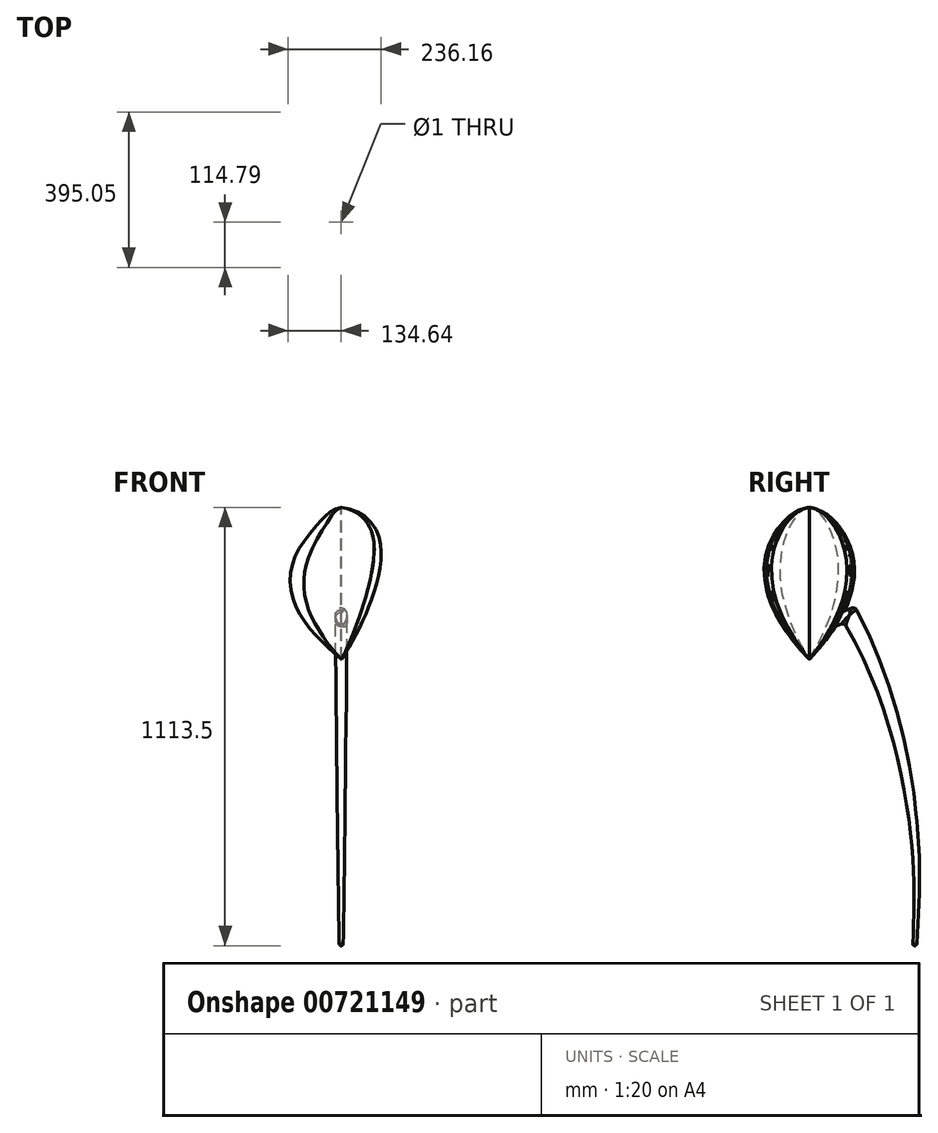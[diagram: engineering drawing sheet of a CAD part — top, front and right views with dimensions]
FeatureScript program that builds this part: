
annotation { "Feature Type Name" : "Feature", "Feature Type Description" : "" }
export const myFeature = defineFeature(function(context is Context, id is Id, definition is map)
    precondition{}
    {
        {
            var Q0;
            Q0=qCreatedBy(makeId("Top.planeOp"),FACE);
            var sketch = newSketch(context, id + "F0", { "sketchPlane" : qUnion([Q0])});
            skCircle(sketch, "E0", {"center": v(0, 0) * mm, "radius": 83.85 * mm, "construction": true});
            skArc(sketch, "E1", {"start": v(12.92, 91.47) * mm, "mid": v(7.44, 96.88) * mm, "end": v(0, 98.85) * mm});
            skLineSegment(sketch, "E2", {"start": v(0, 0) * mm, "end": v(0, 114.42) * mm, "construction": true});
            skLineSegment(sketch, "E3", {"start": v(0, 0) * mm, "end": v(123.6, 0) * mm, "construction": true});
            skArc(sketch, "E4.1.0", {"start": v(40.56, 83) * mm, "mid": v(30.55, 94.01) * mm, "end": v(15.97, 90.98) * mm});
            skArc(sketch, "E4.2.0", {"start": v(64.22, 66.4) * mm, "mid": v(58.1, 79.97) * mm, "end": v(43.3, 81.6) * mm});
            skArc(sketch, "E4.3.0", {"start": v(81.6, 43.3) * mm, "mid": v(79.97, 58.1) * mm, "end": v(66.4, 64.22) * mm});
            skArc(sketch, "E4.4.0", {"start": v(90.98, 15.97) * mm, "mid": v(94.01, 30.55) * mm, "end": v(83, 40.56) * mm});
            skArc(sketch, "E4.5.0", {"start": v(98.85, 0) * mm, "mid": v(96.88, 7.44) * mm, "end": v(91.47, 12.92) * mm});
            skLineSegment(sketch, "E4.anchor1", {"start": v(0, 0) * mm, "end": v(0, 83.85) * mm, "construction": true});
            skLineSegment(sketch, "E4.anchor2", {"start": v(0, 0) * mm, "end": v(83.85, 0) * mm, "construction": true});
            skPoint(sketch, "E5.visualSharp", {"position": v(14.1, 88.99) * mm});
            skArc(sketch, "E5.filletArc", {"start": v(12.92, 91.47) * mm, "mid": v(14.33, 90.5) * mm, "end": v(15.97, 90.98) * mm});
            skPoint(sketch, "E6.visualSharp", {"position": v(40.9, 80.28) * mm});
            skArc(sketch, "E6.filletArc", {"start": v(40.56, 83) * mm, "mid": v(41.6, 81.65) * mm, "end": v(43.3, 81.6) * mm});
            skPoint(sketch, "E7.visualSharp", {"position": v(63.7, 63.7) * mm});
            skArc(sketch, "E7.filletArc", {"start": v(64.22, 66.4) * mm, "mid": v(64.8, 64.8) * mm, "end": v(66.4, 64.22) * mm});
            skPoint(sketch, "E8.visualSharp", {"position": v(80.28, 40.9) * mm});
            skArc(sketch, "E8.filletArc", {"start": v(81.6, 43.3) * mm, "mid": v(81.65, 41.6) * mm, "end": v(83, 40.56) * mm});
            skPoint(sketch, "E9.visualSharp", {"position": v(88.99, 14.1) * mm});
            skArc(sketch, "E9.filletArc", {"start": v(90.98, 15.97) * mm, "mid": v(90.5, 14.33) * mm, "end": v(91.47, 12.92) * mm});
            skArc(sketch, "E10.MirrorCS", {"start": v(-12.92, 91.47) * mm, "mid": v(-7.44, 96.88) * mm, "end": v(0, 98.85) * mm});
            skArc(sketch, "E11.MirrorCS", {"start": v(-40.56, 83) * mm, "mid": v(-30.55, 94.01) * mm, "end": v(-15.97, 90.98) * mm});
            skArc(sketch, "E12.MirrorCS", {"start": v(-64.22, 66.4) * mm, "mid": v(-58.1, 79.97) * mm, "end": v(-43.3, 81.6) * mm});
            skArc(sketch, "E13.MirrorCS", {"start": v(-81.6, 43.3) * mm, "mid": v(-79.97, 58.1) * mm, "end": v(-66.4, 64.22) * mm});
            skArc(sketch, "E14.MirrorCS", {"start": v(-90.98, 15.97) * mm, "mid": v(-94.01, 30.55) * mm, "end": v(-83, 40.56) * mm});
            skArc(sketch, "E15.MirrorCS", {"start": v(-98.85, 0) * mm, "mid": v(-96.88, 7.44) * mm, "end": v(-91.47, 12.92) * mm});
            skArc(sketch, "E16.MirrorCS", {"start": v(-12.92, 91.47) * mm, "mid": v(-14.33, 90.5) * mm, "end": v(-15.97, 90.98) * mm});
            skPoint(sketch, "E17.MirrorP", {"position": v(-14.1, 88.99) * mm});
            skArc(sketch, "E18.MirrorCS", {"start": v(-40.56, 83) * mm, "mid": v(-41.6, 81.65) * mm, "end": v(-43.3, 81.6) * mm});
            skPoint(sketch, "E19.MirrorP", {"position": v(-40.9, 80.28) * mm});
            skArc(sketch, "E20.MirrorCS", {"start": v(-64.22, 66.4) * mm, "mid": v(-64.8, 64.8) * mm, "end": v(-66.4, 64.22) * mm});
            skPoint(sketch, "E21.MirrorP", {"position": v(-80.28, 40.9) * mm});
            skArc(sketch, "E22.MirrorCS", {"start": v(-81.6, 43.3) * mm, "mid": v(-81.65, 41.6) * mm, "end": v(-83, 40.56) * mm});
            skArc(sketch, "E23.MirrorCS", {"start": v(-90.98, 15.97) * mm, "mid": v(-90.5, 14.33) * mm, "end": v(-91.47, 12.92) * mm});
            skPoint(sketch, "E24.MirrorP", {"position": v(-88.99, 14.1) * mm});
            skArc(sketch, "E25.MirrorCS", {"start": v(40.56, -83) * mm, "mid": v(41.6, -81.65) * mm, "end": v(43.3, -81.6) * mm});
            skArc(sketch, "E26.MirrorCS", {"start": v(-12.92, -91.47) * mm, "mid": v(-14.33, -90.5) * mm, "end": v(-15.97, -90.98) * mm});
            skArc(sketch, "E27.MirrorCS", {"start": v(-40.56, -83) * mm, "mid": v(-41.6, -81.65) * mm, "end": v(-43.3, -81.6) * mm});
            skArc(sketch, "E28.MirrorCS", {"start": v(-81.6, -43.3) * mm, "mid": v(-81.65, -41.6) * mm, "end": v(-83, -40.56) * mm});
            skArc(sketch, "E29.MirrorCS", {"start": v(12.92, -91.47) * mm, "mid": v(14.33, -90.5) * mm, "end": v(15.97, -90.98) * mm});
            skArc(sketch, "E30.MirrorCS", {"start": v(-90.98, -15.97) * mm, "mid": v(-90.5, -14.33) * mm, "end": v(-91.47, -12.92) * mm});
            skArc(sketch, "E31.MirrorCS", {"start": v(64.22, -66.4) * mm, "mid": v(64.8, -64.8) * mm, "end": v(66.4, -64.22) * mm});
            skArc(sketch, "E32.MirrorCS", {"start": v(81.6, -43.3) * mm, "mid": v(81.65, -41.6) * mm, "end": v(83, -40.56) * mm});
            skArc(sketch, "E33.MirrorCS", {"start": v(90.98, -15.97) * mm, "mid": v(90.5, -14.33) * mm, "end": v(91.47, -12.92) * mm});
            skArc(sketch, "E34.MirrorCS", {"start": v(-64.22, -66.4) * mm, "mid": v(-64.8, -64.8) * mm, "end": v(-66.4, -64.22) * mm});
            skPoint(sketch, "E35.MirrorP", {"position": v(40.9, -80.28) * mm});
            skArc(sketch, "E36.MirrorCS", {"start": v(-64.22, -66.4) * mm, "mid": v(-58.1, -79.97) * mm, "end": v(-43.3, -81.6) * mm});
            skArc(sketch, "E37.MirrorCS", {"start": v(-90.98, -15.97) * mm, "mid": v(-94.01, -30.55) * mm, "end": v(-83, -40.56) * mm});
            skPoint(sketch, "E38.MirrorP", {"position": v(-80.28, -40.9) * mm});
            skPoint(sketch, "E39.MirrorP", {"position": v(-40.9, -80.28) * mm});
            skPoint(sketch, "E40.MirrorP", {"position": v(-88.99, -14.1) * mm});
            skArc(sketch, "E41.MirrorCS", {"start": v(40.56, -83) * mm, "mid": v(30.55, -94.01) * mm, "end": v(15.97, -90.98) * mm});
            skArc(sketch, "E42.MirrorCS", {"start": v(-81.6, -43.3) * mm, "mid": v(-79.97, -58.1) * mm, "end": v(-66.4, -64.22) * mm});
            skArc(sketch, "E43.MirrorCS", {"start": v(81.6, -43.3) * mm, "mid": v(79.97, -58.1) * mm, "end": v(66.4, -64.22) * mm});
            skArc(sketch, "E44.MirrorCS", {"start": v(64.22, -66.4) * mm, "mid": v(58.1, -79.97) * mm, "end": v(43.3, -81.6) * mm});
            skArc(sketch, "E45.MirrorCS", {"start": v(-40.56, -83) * mm, "mid": v(-30.55, -94.01) * mm, "end": v(-15.97, -90.98) * mm});
            skPoint(sketch, "E46.MirrorP", {"position": v(63.7, -63.7) * mm});
            skPoint(sketch, "E47.MirrorP", {"position": v(-14.1, -88.99) * mm});
            skArc(sketch, "E48.MirrorCS", {"start": v(90.98, -15.97) * mm, "mid": v(94.01, -30.55) * mm, "end": v(83, -40.56) * mm});
            skPoint(sketch, "E49.MirrorP", {"position": v(88.99, -14.1) * mm});
            skPoint(sketch, "E50.MirrorP", {"position": v(14.1, -88.99) * mm});
            skPoint(sketch, "E51.MirrorP", {"position": v(80.28, -40.9) * mm});
            skArc(sketch, "E52.MirrorCS", {"start": v(-12.92, -91.47) * mm, "mid": v(-7.44, -96.88) * mm, "end": v(0, -98.85) * mm});
            skArc(sketch, "E53.MirrorCS", {"start": v(12.92, -91.47) * mm, "mid": v(7.44, -96.88) * mm, "end": v(0, -98.85) * mm});
            skArc(sketch, "E54.MirrorCS", {"start": v(98.85, 0) * mm, "mid": v(96.88, -7.44) * mm, "end": v(91.47, -12.92) * mm});
            skArc(sketch, "E55.MirrorCS", {"start": v(-98.85, 0) * mm, "mid": v(-96.88, -7.44) * mm, "end": v(-91.47, -12.92) * mm});
            skSolve(sketch);
        }
        {
            var Q0;
            Q0=qCreatedBy(makeId("Top.planeOp"),FACE);
            cPlane(context, id + "F1", {"entities" : qUnion([Q0]), "cplaneType" : CPlaneType.OFFSET, "offset" : 86 * mm, "width" : 150 * mm, "height" : 150 * mm});
        }
        {
            var Q0;
            Q0=qCreatedBy(makeId("Top.planeOp"),FACE);
            cPlane(context, id + "F2", {"entities" : qUnion([Q0]), "cplaneType" : CPlaneType.OFFSET, "offset" : 300 * mm, "oppositeDirection" : true, "width" : 150 * mm, "height" : 150 * mm});
        }
        {
            var Q0;
            Q0=qCreatedBy(id+"F2.planeOp",FACE);
            var sketch = newSketch(context, id + "F3", { "sketchPlane" : qUnion([Q0])});
            skPoint(sketch, "E56", {"position": v(0, 0) * mm});
            skSolve(sketch);
        }
        {
            var Q0;
            Q0=qCreatedBy(id+"F1.planeOp",FACE);
            var sketch = newSketch(context, id + "F4", { "sketchPlane" : qUnion([Q0])});
            skPoint(sketch, "E57", {"position": v(0, 0) * mm});
            skSolve(sketch);
        }
        {
            var Q0;
            Q0=qCreatedBy(makeId("Front.planeOp"),FACE);
            var sketch = newSketch(context, id + "F5", { "sketchPlane" : qUnion([Q0])});
            skFitSpline(sketch, "E58", {"points": [v(0, 86) * mm, v(98.85, 0) * mm, v(0, -300) * mm], "startDerivative": vector(346.65, -37.83) * mm, "endDerivative": vector(-262.13, -379.76) * mm});
            skLineSegment(sketch, "E59", {"start": v(0, 86) * mm, "end": v(0, 114.17) * mm, "construction": true});
            skSolve(sketch);
        }
        {
            var Q0;
            Q0=sQuery(id+"F4.wireOp",VERTEX,"E57");
            var Q1;
            Q1=makeQuery(id+"F0.imprint","IMPRINT",FACE,{"disambiguationData":[TD([[makeQuery(id+"F0.imprint","IMPRINT",EDGE,{"derivedFrom":sQuery(id+"F0.wireOp",EDGE,"E1")}),1.0]])]});
            var Q2;
            Q2=sQuery(id+"F3.wireOp",VERTEX,"E56");
            var Q3;
            Q3=sQuery(id+"FytwGCAa7eDT9YU_0.2.F5.wireOp",EDGE,"E58");
            var Q4;
            Q4=sQuery(id+"F5.wireOp",EDGE,"E58");
            var Q5;
            Q5=sQuery(id+"FytwGCAa7eDT9YU_0.3.F5.wireOp",EDGE,"E58");
            var Q6;
            Q6=sQuery(id+"FytwGCAa7eDT9YU_0.1.F5.wireOp",EDGE,"E58");
            loft(context, id + "F6", {"addGuides" : true, "sheetProfilesArray" : [{ "sheetProfileEntities" : qUnion([Q0]) }, { "sheetProfileEntities" : qUnion([Q1]) }, { "sheetProfileEntities" : qUnion([Q2]) }], "guidesArray" : [{ "guideEntities" : qUnion([Q3]), "guideDerivativeType" : LoftGuideDerivativeType.DEFAULT, "guideDerivativeMagnitude" : 1 }, { "guideEntities" : qUnion([Q4]), "guideDerivativeType" : LoftGuideDerivativeType.DEFAULT, "guideDerivativeMagnitude" : 1 }, { "guideEntities" : qUnion([Q5]), "guideDerivativeType" : LoftGuideDerivativeType.DEFAULT, "guideDerivativeMagnitude" : 1 }, { "guideEntities" : qUnion([Q6]), "guideDerivativeType" : LoftGuideDerivativeType.DEFAULT, "guideDerivativeMagnitude" : 1 }]});
        }
        {
            var Q0;
            Q0=qCreatedBy(makeId("Front.planeOp"),FACE);
            var sketch = newSketch(context, id + "F7", { "sketchPlane" : qUnion([Q0])});
            skLineSegment(sketch, "E60", {"start": v(0, 0) * mm, "end": v(0, -301.96) * mm, "construction": true});
            skCircle(sketch, "E61", {"center": v(0, -227.47) * mm, "radius": 15 * mm});
            skSolve(sketch);
        }
        {
            var Q0;
            Q0=qCreatedBy(makeId("Right.planeOp"),FACE);
            var sketch = newSketch(context, id + "F8", { "sketchPlane" : qUnion([Q0])});
            skLineSegment(sketch, "E62", {"start": v(0, -227.47) * mm, "end": v(122.28, -179.04) * mm});
            skSolve(sketch);
        }
        {
            var Q0;
            Q0 = qSketchRegion(id + "F7", true);
            var Q1;
            Q1=sQuery(id+"F8.wireOp",EDGE,"E62");
            sweep(context, id + "F9", {"profiles" : qUnion([Q0]), "path" : qUnion([Q1])});
        }
        {
            var Q0;
            Q0=qCreatedBy(makeId("Right.planeOp"),FACE);
            var sketch = newSketch(context, id + "F10", { "sketchPlane" : qUnion([Q0])});
            skLineSegment(sketch, "E63", {"start": v(73.97, -229.82) * mm, "end": v(137.22, -134.55) * mm});
            skLineSegment(sketch, "E64", {"start": v(137.22, -134.55) * mm, "end": v(177.46, -206) * mm});
            skLineSegment(sketch, "E65", {"start": v(177.46, -206) * mm, "end": v(73.97, -229.82) * mm});
            skSolve(sketch);
        }
        {
            var Q0;
            Q0 = qSketchRegion(id + "F10", true);
            extrude(context, id + "F11", {"entities" : qUnion([Q0]), "operationType" : NewBodyOperationType.REMOVE, "endBound" : BoundingType.SYMMETRIC, "depth" : 57.6 * mm, "offsetDistance" : 25 * mm});
        }
        {
            var Q0;
            Q0=qCreatedBy(makeId("Right.planeOp"),FACE);
            var sketch = newSketch(context, id + "F12", { "sketchPlane" : qUnion([Q0])});
            skFitSpline(sketch, "E66", {"points": [v(88.97, -207.23) * mm, v(260.19, -772.02) * mm, v(262.67, -1027.56) * mm], "startDerivative": vector(568.67, -966.09) * mm, "endDerivative": vector(-27.43, -584.73) * mm});
            skSolve(sketch);
        }
        {
            var Q0;
            Q0=sQuery(id+"F12.wireOp",VERTEX,"E66.end");
            var Q1;
            Q1=qCreatedBy(makeId("Top.planeOp"),FACE);
            cPlane(context, id + "F13", {"entities" : qUnion([Q0, Q1]), "cplaneType" : CPlaneType.PLANE_POINT, "offset" : 25 * mm, "width" : 150 * mm, "height" : 150 * mm});
        }
        {
            var Q0;
            Q0=qCreatedBy(id+"F13.planeOp",FACE);
            var sketch = newSketch(context, id + "F14", { "sketchPlane" : qUnion([Q0])});
            skCircle(sketch, "E67", {"center": v(0, 267.67) * mm, "radius": 5 * mm});
            skLineSegment(sketch, "E68", {"start": v(0, 267.67) * mm, "end": v(0, 262.67) * mm, "construction": true});
            skSolve(sketch);
        }
        {
            var Q0;
            Q0=makeQuery(id+"F14.imprint","IMPRINT",FACE,{"disambiguationData":[TD([[makeQuery(id+"F14.imprint","IMPRINT",EDGE,{"derivedFrom":sQuery(id+"F14.wireOp",EDGE,"E67")}),1.0]])]});
            var Q1;
            Q1=makeQuery(id+"F11.boolean.opBoolean","COPY",FACE,{"derivedFrom":makeQuery(id+"F11.opExtrude","SWEPT_FACE",FACE,{"disambiguationData":[OSD([sQuery(id+"F10.wireOp",EDGE,"E63")])]})});
            var Q2;
            Q2=sQuery(id+"F12.wireOp",EDGE,"E66");
            loft(context, id + "F15", {"addGuides" : true, "sheetProfilesArray" : [{ "sheetProfileEntities" : qUnion([Q0]) }, { "sheetProfileEntities" : qUnion([Q1]) }], "guidesArray" : [{ "guideEntities" : qUnion([Q2]), "guideDerivativeType" : LoftGuideDerivativeType.DEFAULT, "guideDerivativeMagnitude" : 1 }]});
        }
        {
            var Q0;
            Q0=makeQuery(id+"F6.opLoft","SWEPT_BODY",BODY,{"disambiguationData":[OSD([sQuery(id+"F0.wireOp",EDGE,"E33.MirrorCS"),sQuery(id+"F3.wireOp",VERTEX,"E56"),sQuery(id+"F4.wireOp",VERTEX,"E57"),sQuery(id+"F5.wireOp",EDGE,"E58"),sQuery(id+"FytwGCAa7eDT9YU_0.1.F5.wireOp",EDGE,"E58"),sQuery(id+"FytwGCAa7eDT9YU_0.2.F5.wireOp",EDGE,"E58"),sQuery(id+"FytwGCAa7eDT9YU_0.3.F5.wireOp",EDGE,"E58")])]});
            var Q1;
            Q1=makeQuery(id+"FHNdmcrHpAsNhch_2.2.F9.opSweep","SWEPT_BODY",BODY,{"disambiguationData":[OSD([sQuery(id+"F7.wireOp",EDGE,"E61"),sQuery(id+"F8.wireOp",EDGE,"E62")])]});
            var Q2;
            Q2=makeQuery(id+"F9.opSweep","SWEPT_BODY",BODY,{"disambiguationData":[OSD([sQuery(id+"F7.wireOp",EDGE,"E61"),sQuery(id+"F8.wireOp",EDGE,"E62")])]});
            var Q3;
            Q3=makeQuery(id+"FHNdmcrHpAsNhch_2.1.F9.opSweep","SWEPT_BODY",BODY,{"disambiguationData":[OSD([sQuery(id+"F7.wireOp",EDGE,"E61"),sQuery(id+"F8.wireOp",EDGE,"E62")])]});
            var Q4;
            Q4=makeQuery(id+"FAWmEOz5LhCQqlK_3.1.F15.opLoft","SWEPT_BODY",BODY,{"disambiguationData":[OSD([sQuery(id+"F10.wireOp",EDGE,"E63"),sQuery(id+"F12.wireOp",EDGE,"E66"),makeQuery(id+"F14.imprint","IMPRINT",FACE,{"disambiguationData":[TD([[makeQuery(id+"F14.imprint","IMPRINT",EDGE,{"derivedFrom":sQuery(id+"F14.wireOp",EDGE,"E67")}),1.0]])]})])]});
            var Q5;
            Q5=makeQuery(id+"F15.opLoft","SWEPT_BODY",BODY,{"disambiguationData":[OSD([sQuery(id+"F10.wireOp",EDGE,"E63"),sQuery(id+"F12.wireOp",EDGE,"E66"),makeQuery(id+"F14.imprint","IMPRINT",FACE,{"disambiguationData":[TD([[makeQuery(id+"F14.imprint","IMPRINT",EDGE,{"derivedFrom":sQuery(id+"F14.wireOp",EDGE,"E67")}),1.0]])]})])]});
            var Q6;
            Q6=makeQuery(id+"FAWmEOz5LhCQqlK_3.2.F15.opLoft","SWEPT_BODY",BODY,{"disambiguationData":[OSD([sQuery(id+"F10.wireOp",EDGE,"E63"),sQuery(id+"F12.wireOp",EDGE,"E66"),makeQuery(id+"F14.imprint","IMPRINT",FACE,{"disambiguationData":[TD([[makeQuery(id+"F14.imprint","IMPRINT",EDGE,{"derivedFrom":sQuery(id+"F14.wireOp",EDGE,"E67")}),1.0]])]})])]});
            booleanBodies(context, id + "F16", {"operationType" : BooleanOperationType.UNION, "tools" : qUnion([Q0, Q1, Q2, Q3, Q4, Q5, Q6])});
        }
        {
            var Q0;
            {var subQ0=sQuery(id+"F10.wireOp",EDGE,"E63");var subQ1=sQuery(id+"F8.wireOp",EDGE,"E62");var subQ2=sQuery(id+"F7.wireOp",EDGE,"E61");Q0=makeQuery(id+"F16.opBoolean","MERGE",EDGE,{"derivedFrom":[makeQuery(id+"F11.boolean.opBoolean","INTERSECT",EDGE,{"derivedFrom":[makeQuery(id+"F9.opSweep","SWEPT_FACE",FACE,{"disambiguationData":[OSD([subQ2,subQ1])]}),makeQuery(id+"F11.opExtrude","SWEPT_FACE",FACE,{"disambiguationData":[OSD([subQ0])]})]}),makeQuery(id+"F15.opLoft","MID_CAP_EDGE",EDGE,{"disambiguationData":[OSD([subQ2,subQ1,subQ0,sQuery(id+"F12.wireOp",EDGE,"E66")])],"capPos":1.0})]});}
            var Q1;
            {var subQ0=sQuery(id+"F10.wireOp",EDGE,"E63");var subQ1=sQuery(id+"F8.wireOp",EDGE,"E62");var subQ2=sQuery(id+"F7.wireOp",EDGE,"E61");Q1=makeQuery(id+"F16.opBoolean","MERGE",EDGE,{"derivedFrom":[makeQuery(id+"FHNdmcrHpAsNhch_2.2.F11.boolean.opBoolean","INTERSECT",EDGE,{"derivedFrom":[makeQuery(id+"FHNdmcrHpAsNhch_2.2.F9.opSweep","SWEPT_FACE",FACE,{"disambiguationData":[OSD([subQ2,subQ1])]}),makeQuery(id+"FHNdmcrHpAsNhch_2.2.F11.opExtrude","SWEPT_FACE",FACE,{"disambiguationData":[OSD([subQ0])]})]}),makeQuery(id+"FAWmEOz5LhCQqlK_3.2.F15.opLoft","MID_CAP_EDGE",EDGE,{"disambiguationData":[OSD([subQ2,subQ1,subQ0,sQuery(id+"F12.wireOp",EDGE,"E66")])],"capPos":1.0})]});}
            var Q2;
            {var subQ0=sQuery(id+"F10.wireOp",EDGE,"E63");var subQ1=sQuery(id+"F8.wireOp",EDGE,"E62");var subQ2=sQuery(id+"F7.wireOp",EDGE,"E61");Q2=makeQuery(id+"F16.opBoolean","MERGE",EDGE,{"derivedFrom":[makeQuery(id+"FHNdmcrHpAsNhch_2.1.F11.boolean.opBoolean","INTERSECT",EDGE,{"derivedFrom":[makeQuery(id+"FHNdmcrHpAsNhch_2.1.F9.opSweep","SWEPT_FACE",FACE,{"disambiguationData":[OSD([subQ2,subQ1])]}),makeQuery(id+"FHNdmcrHpAsNhch_2.1.F11.opExtrude","SWEPT_FACE",FACE,{"disambiguationData":[OSD([subQ0])]})]}),makeQuery(id+"FAWmEOz5LhCQqlK_3.1.F15.opLoft","MID_CAP_EDGE",EDGE,{"disambiguationData":[OSD([subQ2,subQ1,subQ0,sQuery(id+"F12.wireOp",EDGE,"E66")])],"capPos":1.0})]});}
            fillet(context, id + "F17", {"entities" : qUnion([Q0, Q1, Q2]), "radius" : 10 * mm, "tangentPropagation" : true, "allowEdgeOverflow" : false});
        }
        {
            var Q0;
            Q0=makeQuery(id+"FAWmEOz5LhCQqlK_3.1.F15.opLoft","MID_CAP_EDGE",EDGE,{"disambiguationData":[OSD([sQuery(id+"F12.wireOp",EDGE,"E66"),sQuery(id+"F14.wireOp",EDGE,"E67")])],"capPos":0.0});
            var Q1;
            Q1=makeQuery(id+"FAWmEOz5LhCQqlK_3.2.F15.opLoft","MID_CAP_EDGE",EDGE,{"disambiguationData":[OSD([sQuery(id+"F12.wireOp",EDGE,"E66"),sQuery(id+"F14.wireOp",EDGE,"E67")])],"capPos":0.0});
            var Q2;
            Q2=makeQuery(id+"F15.opLoft","MID_CAP_EDGE",EDGE,{"disambiguationData":[OSD([sQuery(id+"F12.wireOp",EDGE,"E66"),sQuery(id+"F14.wireOp",EDGE,"E67")])],"capPos":0.0});
            fillet(context, id + "F18", {"entities" : qUnion([Q0, Q1, Q2]), "radius" : 5 * mm, "tangentPropagation" : true, "allowEdgeOverflow" : false});
        }
        {
            var Q0;
            Q0=qCreatedBy(id+"F1.planeOp",FACE);
            var sketch = newSketch(context, id + "F19", { "sketchPlane" : qUnion([Q0])});
            skCircle(sketch, "E69", {"center": v(0, 0) * mm, "radius": 0.5 * mm});
            skSolve(sketch);
        }
        {
            var Q0;
            Q0 = qSketchRegion(id + "F19", true);
            extrude(context, id + "F20", {"entities" : qUnion([Q0]), "operationType" : NewBodyOperationType.REMOVE, "oppositeDirection" : true, "depth" : 390 * mm, "offsetDistance" : 25 * mm});
        }
    });
